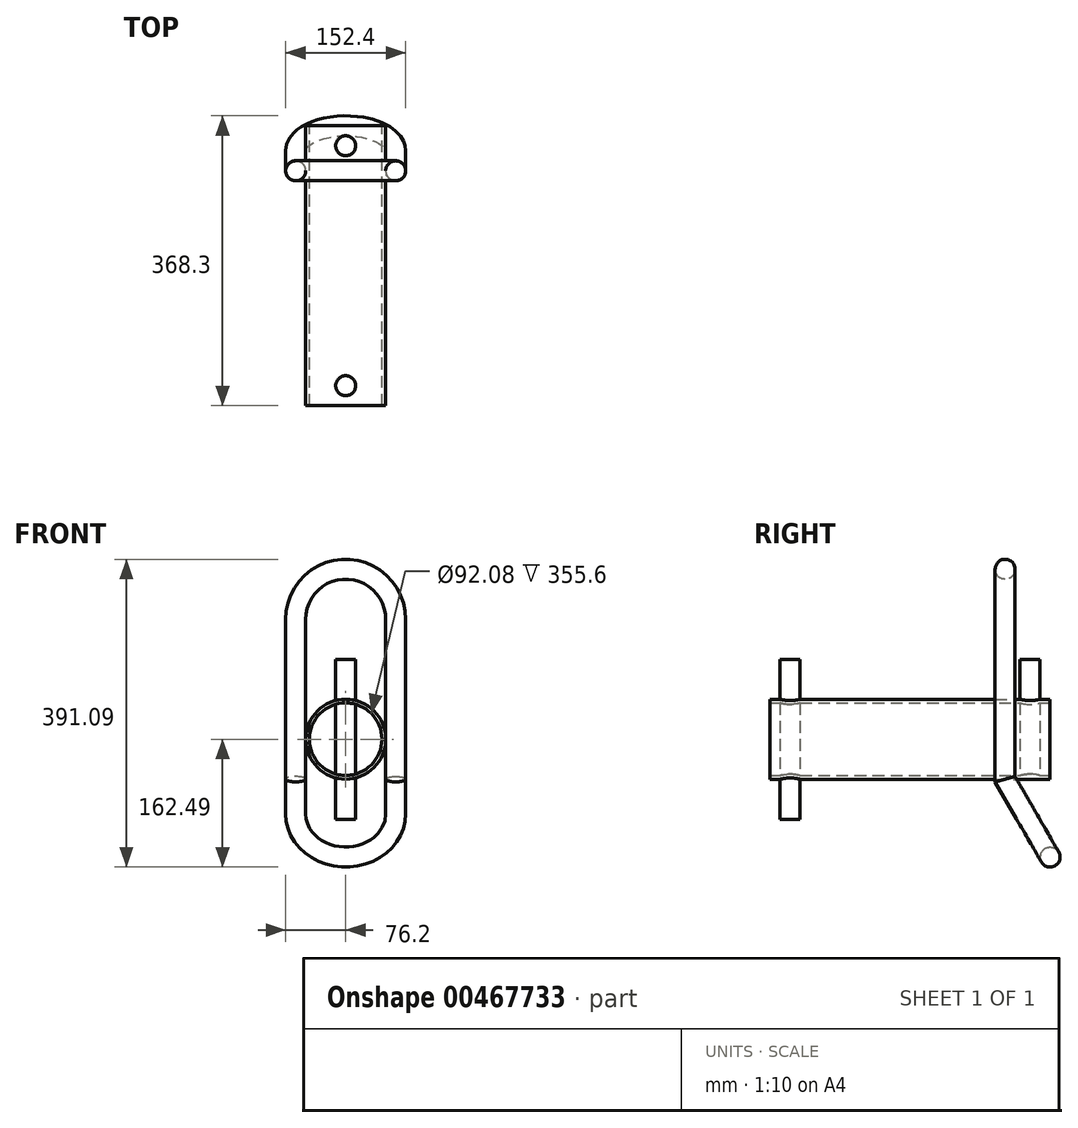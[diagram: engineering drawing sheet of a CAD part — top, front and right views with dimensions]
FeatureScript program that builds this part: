
annotation { "Feature Type Name" : "Feature", "Feature Type Description" : "" }
export const myFeature = defineFeature(function(context is Context, id is Id, definition is map)
    precondition{}
    {
        {
            var Q0;
            Q0=qCreatedBy(makeId("Front.planeOp"),FACE);
            var sketch = newSketch(context, id + "F0", { "sketchPlane" : qUnion([Q0])});
            skCircle(sketch, "E0", {"center": v(0, 0) * mm, "radius": 50.8 * mm});
            skCircle(sketch, "E1", {"center": v(0, 0) * mm, "radius": 46.04 * mm});
            skSolve(sketch);
        }
        {
            var Q0;
            Q0=makeQuery(id+"F0.imprint","IMPRINT",FACE,{"disambiguationData":[TD([[makeQuery(id+"F0.imprint","IMPRINT",EDGE,{"derivedFrom":sQuery(id+"F0.wireOp",EDGE,"E0")}),1.0]])]});
            var Q1;
            Q1=sQuery(id+"F0.wireOp",EDGE,"E1");
            var Q2;
            Q2=sQuery(id+"F0.wireOp",EDGE,"E0");
            extrude(context, id + "F1", {"entities" : qUnion([Q0]), "surfaceEntities" : qUnion([Q1, Q2]), "endBound" : BoundingType.SYMMETRIC, "depth" : 355.6 * mm});
        }
        {
            var Q0;
            Q0=qCreatedBy(makeId("Top.planeOp"),FACE);
            var sketch = newSketch(context, id + "F2", { "sketchPlane" : qUnion([Q0])});
            skCircle(sketch, "E2", {"center": v(0, 152.4) * mm, "radius": 12.7 * mm});
            skSolve(sketch);
        }
        {
            var Q0;
            Q0=makeQuery(id+"F2.imprint","IMPRINT",FACE,{"disambiguationData":[TD([[makeQuery(id+"F2.imprint","IMPRINT",EDGE,{"derivedFrom":sQuery(id+"F2.wireOp",EDGE,"E2")}),1.0]])]});
            var Q1;
            Q1=sQuery(id+"F2.wireOp",EDGE,"E2");
            extrude(context, id + "F3", {"entities" : qUnion([Q0]), "surfaceEntities" : qUnion([Q1]), "depth" : 101.6 * mm});
        }
        {
            var Q0;
            Q0=makeQuery(id+"F3.opExtrude","CAP_FACE",FACE,{"disambiguationData":[OSD([sQuery(id+"F2.wireOp",EDGE,"E2")])],"isStart":true});
            extrude(context, id + "F4", {"entities" : qUnion([Q0]), "operationType" : NewBodyOperationType.ADD, "endBound" : BoundingType.UP_TO_NEXT, "depth" : 25.4 * mm});
        }
        {
            var Q0;
            Q0=qCreatedBy(makeId("Top.planeOp"),FACE);
            var sketch = newSketch(context, id + "F5", { "sketchPlane" : qUnion([Q0])});
            skCircle(sketch, "E3", {"center": v(0, -152.4) * mm, "radius": 12.7 * mm});
            skSolve(sketch);
        }
        {
            var Q0;
            Q0=makeQuery(id+"F5.imprint","IMPRINT",FACE,{"disambiguationData":[TD([[makeQuery(id+"F5.imprint","IMPRINT",EDGE,{"derivedFrom":sQuery(id+"F5.wireOp",EDGE,"E3")}),1.0]])]});
            var Q1;
            Q1=sQuery(id+"F5.wireOp",EDGE,"E3");
            extrude(context, id + "F6", {"entities" : qUnion([Q0]), "operationType" : NewBodyOperationType.ADD, "surfaceEntities" : qUnion([Q1]), "endBound" : BoundingType.SYMMETRIC, "depth" : 203.2 * mm});
        }
        {
            var Q0;
            Q0=qCreatedBy(makeId("Front.planeOp"),FACE);
            cPlane(context, id + "F7", {"entities" : qUnion([Q0]), "cplaneType" : CPlaneType.OFFSET, "offset" : 120.65 * mm, "oppositeDirection" : true, "width" : 152.4 * mm, "height" : 152.4 * mm});
        }
        {
            var Q0;
            Q0=qCreatedBy(id+"F7.planeOp",FACE);
            var sketch = newSketch(context, id + "F8", { "sketchPlane" : qUnion([Q0])});
            skLineSegment(sketch, "E4", {"start": v(63.5, 0) * mm, "end": v(63.5, 152.4) * mm});
            skLineSegment(sketch, "E5", {"start": v(0, 0) * mm, "end": v(0, -143) * mm, "construction": true});
            skLineSegment(sketch, "E6", {"start": v(63.5, 0) * mm, "end": v(63.5, -50.8) * mm});
            skLineSegment(sketch, "E7", {"start": v(-63.5, 152.4) * mm, "end": v(-63.5, 0) * mm});
            skLineSegment(sketch, "E8", {"start": v(-63.5, 0) * mm, "end": v(-63.5, -50.8) * mm});
            skArc(sketch, "E9", {"start": v(63.5, 152.4) * mm, "mid": v(0, 215.9) * mm, "end": v(-63.5, 152.4) * mm});
            skLineSegment(sketch, "E10", {"start": v(63.5, -50.8) * mm, "end": v(-63.5, -50.8) * mm, "construction": true});
            skSolve(sketch);
        }
        {
            var Q0;
            Q0=sQuery(id+"F8.wireOp",EDGE,"E10");
            cPlane(context, id + "F9", {"entities" : qUnion([Q0]), "cplaneType" : CPlaneType.LINE_ANGLE, "offset" : 25.4 * mm, "angle" : 30 * degree, "oppositeDirection" : true, "width" : 152.4 * mm, "height" : 152.4 * mm});
        }
        {
            var Q0;
            Q0=qCreatedBy(id+"F9.planeOp",FACE);
            var sketch = newSketch(context, id + "F10", { "sketchPlane" : qUnion([Q0])});
            skLineSegment(sketch, "E11", {"start": v(63.5, -104.32) * mm, "end": v(63.5, -155.12) * mm});
            skLineSegment(sketch, "E12", {"start": v(-63.5, -104.32) * mm, "end": v(-63.5, -155.12) * mm});
            skArc(sketch, "E13", {"start": v(63.5, -155.12) * mm, "mid": v(0, -218.62) * mm, "end": v(-63.5, -155.12) * mm});
            skSolve(sketch);
        }
        {
            var Q0;
            Q0=qCreatedBy(makeId("Top.planeOp"),FACE);
            var sketch = newSketch(context, id + "F11", { "sketchPlane" : qUnion([Q0])});
            skCircle(sketch, "E14", {"center": v(-63.5, 120.65) * mm, "radius": 12.7 * mm});
            skSolve(sketch);
        }
        {
            var Q0;
            Q0=makeQuery(id+"F11.imprint","IMPRINT",FACE,{"disambiguationData":[TD([[makeQuery(id+"F11.imprint","IMPRINT",EDGE,{"derivedFrom":sQuery(id+"F11.wireOp",EDGE,"E14")}),1.0]])]});
            var Q1;
            Q1=sQuery(id+"F8.wireOp",EDGE,"E7");
            var Q2;
            Q2=sQuery(id+"F8.wireOp",EDGE,"E9");
            var Q3;
            Q3=sQuery(id+"F8.wireOp",EDGE,"E4");
            var Q4;
            Q4=sQuery(id+"F8.wireOp",EDGE,"E6");
            var Q5;
            Q5=sQuery(id+"F10.wireOp",EDGE,"E11");
            var Q6;
            Q6=sQuery(id+"F10.wireOp",EDGE,"E13");
            var Q7;
            Q7=sQuery(id+"F10.wireOp",EDGE,"E12");
            var Q8;
            Q8=sQuery(id+"F8.wireOp",EDGE,"E8");
            sweep(context, id + "F12", {"profiles" : qUnion([Q0]), "path" : qUnion([Q1, Q2, Q3, Q4, Q5, Q6, Q7, Q8])});
        }
    });
